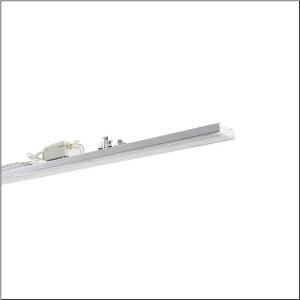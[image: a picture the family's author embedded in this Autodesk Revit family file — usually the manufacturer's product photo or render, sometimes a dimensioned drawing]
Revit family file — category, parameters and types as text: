
# Revit family: licross_21_recessed_mo_52te12dv6fxg3s
name_source: partatom
category: Lighting Fixtures
units: mm (PartAtom-declared; Revit-internal decimal feet)

## family parameters
Cut with Voids When Loaded = No
Host = Face
Light Source = No
Part Type = Normal
Room Calculation Point = No
Round Connector Dimension = Use Diameter
Shared = No

## types (1)
- --- (1 x LED, 920 lm, 5.5 W, 6500K)
    Apparent Load = 6 VA
    CIE Flux Codes = 72 92 99 100 100
    Color Rendering = 80
    Color Temperature = 6500K
    Default Elevation = 1800 mm
    Description = Licross 21 Recessed MO, luminaire insert, of sheet steel, galvanised, coil coated, white, length: 2.250mm, width: 66mm, height: 67mm, LED rated luminous flux: 15.000lm, light colour: 865, SDCM (Standard Deviation of Colour Matching)MacAdam ≤ 3 SDCM (initial), control gear: DALI 2 (for two DALI lines), with plug, 6-pole, with phase selection, for trunking rail, 14-core, mains connection: 220..240V, AC, 50/60Hz, rated input power: 89W, for trunking rail, 14-core, internal wiring halogen-free, for emergency light function, converter,control gear: single battery element, battery: LiFePO4, 9Ah, primary optical cover: cover, of PMMA, light emission: direct distribution, primary light characteristic: symmetric, protection rating (complete): IP54, insulation class (complete): insulation class I (protective earthing), certification: CE, ENEC, VDE, UKCA, protection symbol: D if used in an environment with non-conductive dust loads with corresponding accessories, impact resistance: IK06, permissible ambient temperature for indoor applications: +5..+35°C, standard: EN 60598-2-22, LABS conformity tested according to VDMA 24364:2018-05, reducing of maximum allowable ambient temperature of 5°C with ceiling mounting, corresponds to IFS (International Featured Standards) requirements for safety and quality in the food industry, The light source and the operating device comply with the requirements of the Ecodesign Regulation (EU) 2019/2020 and are replaceable in accordance with this regulation, packaging unit: 1 piece
    Height = 58 mm
    Lamp = 1 x LED
    Lamp Light Flux = 920 lm
    Lamp Power = 5.5 W
    Lamp count = 1
    Length = 2250 mm
    Luminous efficacy = 167 lm/W
    Manufacturer = Siteco
    ModVariant = No
    Model = 52TE12DV6FXG3S
    Mounting Place = Ceiling
    Mounting Type = Pendant
    Number of Poles = 1
    OnlyDefault = Yes
    Power Factor = 1
    Product Name = Licross 21 Recessed MO
    Product group = luminaire insert | ceiling pendant
    ProductGroupID = 901
    Protection Class = Protection class I
    Protection Degree = IP 54
    RLX_Detail_Level = 1
    RLX_Emergency_Light_Flux = 0 lm
    RLX_Emergency_Type = 0
    RLX_Emergency_Type_DB = No
    RlxData = <blob elided: 30409 chars, md5=927482da>
    Socket = socket
    Standby Power = 0 W
    System Light Flux = 920 lm
    System Power = 6 W
    Type Comments = : DC mode (central or group accumulator) initial emergency light level
    Type Image = l_1296930.jpg
    URL = http://relux.com
    VarID = @adj_086901
    Voltage = 0 V
    Weight = 0.00 kg
    Width = 66 mm

## geometry (parser evidence)
native form markers: Blend x4, Sweep x9
no freeform markers — native parametric forms only
